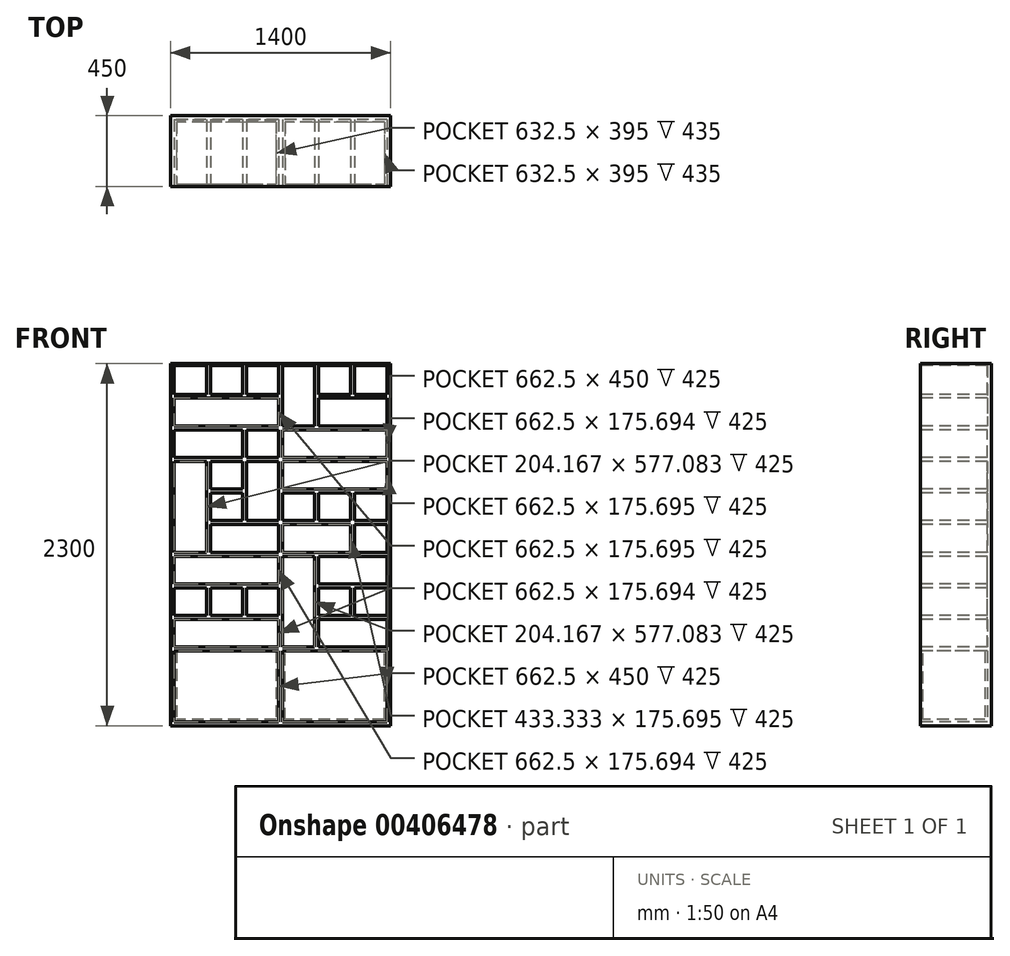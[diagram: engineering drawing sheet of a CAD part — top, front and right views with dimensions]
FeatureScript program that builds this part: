
annotation { "Feature Type Name" : "Feature", "Feature Type Description" : "" }
export const myFeature = defineFeature(function(context is Context, id is Id, definition is map)
    precondition{}
    {
        {
            var Q0;
            Q0=qCreatedBy(makeId("Front.planeOp"),FACE);
            var sketch = newSketch(context, id + "F0", { "sketchPlane" : qUnion([Q0])});
            skLineSegment(sketch, "E0.bottom", {"start": v(-700, 0) * mm, "end": v(700, 0) * mm});
            skLineSegment(sketch, "E0.top", {"start": v(-700, 2300) * mm, "end": v(700, 2300) * mm});
            skLineSegment(sketch, "E0.left", {"start": v(-700, 0) * mm, "end": v(-700, 2300) * mm});
            skLineSegment(sketch, "E0.right", {"start": v(700, 0) * mm, "end": v(700, 2300) * mm});
            skSolve(sketch);
        }
        {
            var Q0;
            Q0=qSketchRegion(id+"F0",true);
            extrude(context, id + "F1", {"entities" : qUnion([Q0]), "depth" : 450 * mm, "offsetDistance" : 25 * mm});
        }
        {
            var Q0;
            Q0=makeQuery(id+"F1.opExtrude","CAP_FACE",FACE,{"disambiguationData":[OSD([sQuery(id+"F0.wireOp",EDGE,"E0.bottom"),sQuery(id+"F0.wireOp",EDGE,"E0.top"),sQuery(id+"F0.wireOp",EDGE,"E0.left"),sQuery(id+"F0.wireOp",EDGE,"E0.right")])],"isStart":false});
            var sketch = newSketch(context, id + "F2", { "sketchPlane" : qUnion([Q0])});
            skLineSegment(sketch, "E1", {"start": v(0, 2300) * mm, "end": v(0, 0) * mm, "construction": true});
            skLineSegment(sketch, "E2.bottom", {"start": v(-675, 25) * mm, "end": v(-12.5, 25) * mm});
            skLineSegment(sketch, "E2.top", {"start": v(-675, 475) * mm, "end": v(-12.5, 475) * mm});
            skLineSegment(sketch, "E2.left", {"start": v(-675, 25) * mm, "end": v(-675, 475) * mm});
            skLineSegment(sketch, "E2.right", {"start": v(-12.5, 25) * mm, "end": v(-12.5, 475) * mm});
            skLineSegment(sketch, "E3.bottom", {"start": v(12.5, 475) * mm, "end": v(675, 475) * mm});
            skLineSegment(sketch, "E3.top", {"start": v(12.5, 25) * mm, "end": v(675, 25) * mm});
            skLineSegment(sketch, "E3.left", {"start": v(12.5, 475) * mm, "end": v(12.5, 25) * mm});
            skLineSegment(sketch, "E3.right", {"start": v(675, 475) * mm, "end": v(675, 25) * mm});
            skLineSegment(sketch, "E4", {"start": v(-700, 487.5) * mm, "end": v(700, 487.5) * mm, "construction": true});
            skLineSegment(sketch, "E5", {"start": v(-700, 1089.58) * mm, "end": v(700, 1089.58) * mm, "construction": true});
            skLineSegment(sketch, "E6", {"start": v(-700, 1691.67) * mm, "end": v(700, 1691.67) * mm, "construction": true});
            skLineSegment(sketch, "E7", {"start": v(-700, 2293.75) * mm, "end": v(700, 2293.75) * mm, "construction": true});
            skLineSegment(sketch, "E8.bottom", {"start": v(-675, 2287.5) * mm, "end": v(-12.5, 2287.5) * mm, "construction": true});
            skLineSegment(sketch, "E8.top", {"start": v(-675, 1704.17) * mm, "end": v(-12.5, 1704.17) * mm, "construction": true});
            skLineSegment(sketch, "E8.left", {"start": v(-675, 2287.5) * mm, "end": v(-675, 1704.17) * mm, "construction": true});
            skLineSegment(sketch, "E8.right", {"start": v(-12.5, 2287.5) * mm, "end": v(-12.5, 1704.17) * mm, "construction": true});
            skLineSegment(sketch, "E9.bottom", {"start": v(-675, 1679.17) * mm, "end": v(-12.5, 1679.17) * mm, "construction": true});
            skLineSegment(sketch, "E9.top", {"start": v(-675, 1102.08) * mm, "end": v(-12.5, 1102.08) * mm, "construction": true});
            skLineSegment(sketch, "E9.left", {"start": v(-675, 1679.17) * mm, "end": v(-675, 1102.08) * mm, "construction": true});
            skLineSegment(sketch, "E9.right", {"start": v(-12.5, 1679.17) * mm, "end": v(-12.5, 1102.08) * mm, "construction": true});
            skLineSegment(sketch, "E10.bottom", {"start": v(-675, 1077.08) * mm, "end": v(-12.5, 1077.08) * mm, "construction": true});
            skLineSegment(sketch, "E10.top", {"start": v(-675, 500) * mm, "end": v(-12.5, 500) * mm, "construction": true});
            skLineSegment(sketch, "E10.left", {"start": v(-675, 1077.08) * mm, "end": v(-675, 500) * mm, "construction": true});
            skLineSegment(sketch, "E10.right", {"start": v(-12.5, 1077.08) * mm, "end": v(-12.5, 500) * mm, "construction": true});
            skLineSegment(sketch, "E11.bottom", {"start": v(12.5, 1077.08) * mm, "end": v(675, 1077.08) * mm, "construction": true});
            skLineSegment(sketch, "E11.top", {"start": v(12.5, 500) * mm, "end": v(675, 500) * mm, "construction": true});
            skLineSegment(sketch, "E11.left", {"start": v(12.5, 1077.08) * mm, "end": v(12.5, 500) * mm, "construction": true});
            skLineSegment(sketch, "E11.right", {"start": v(675, 1077.08) * mm, "end": v(675, 500) * mm, "construction": true});
            skLineSegment(sketch, "E12.bottom", {"start": v(12.5, 1679.17) * mm, "end": v(675, 1679.17) * mm, "construction": true});
            skLineSegment(sketch, "E12.top", {"start": v(12.5, 1102.08) * mm, "end": v(675, 1102.08) * mm, "construction": true});
            skLineSegment(sketch, "E12.left", {"start": v(12.5, 1679.17) * mm, "end": v(12.5, 1102.08) * mm, "construction": true});
            skLineSegment(sketch, "E12.right", {"start": v(675, 1679.17) * mm, "end": v(675, 1102.08) * mm, "construction": true});
            skLineSegment(sketch, "E13.bottom", {"start": v(12.5, 2287.5) * mm, "end": v(675, 2287.5) * mm, "construction": true});
            skLineSegment(sketch, "E13.top", {"start": v(12.5, 1704.17) * mm, "end": v(675, 1704.17) * mm, "construction": true});
            skLineSegment(sketch, "E13.left", {"start": v(12.5, 2287.5) * mm, "end": v(12.5, 1704.17) * mm, "construction": true});
            skLineSegment(sketch, "E13.right", {"start": v(675, 2287.5) * mm, "end": v(675, 1704.17) * mm, "construction": true});
            skLineSegment(sketch, "E14.bottom", {"start": v(12.5, 1704.17) * mm, "end": v(675, 1704.17) * mm});
            skLineSegment(sketch, "E14.top", {"start": v(12.5, 1879.86) * mm, "end": v(675, 1879.86) * mm});
            skLineSegment(sketch, "E14.left", {"start": v(12.5, 1704.17) * mm, "end": v(12.5, 1879.86) * mm});
            skLineSegment(sketch, "E14.right", {"start": v(675, 1704.17) * mm, "end": v(675, 1879.86) * mm});
            skLineSegment(sketch, "E15.bottom", {"start": v(12.5, 1904.86) * mm, "end": v(216.67, 1904.86) * mm});
            skLineSegment(sketch, "E15.top", {"start": v(12.5, 2287.5) * mm, "end": v(216.67, 2287.5) * mm});
            skLineSegment(sketch, "E15.left", {"start": v(12.5, 1904.86) * mm, "end": v(12.5, 2287.5) * mm});
            skLineSegment(sketch, "E15.right", {"start": v(216.67, 1904.86) * mm, "end": v(216.67, 2287.5) * mm});
            skLineSegment(sketch, "E16.bottom", {"start": v(241.67, 1904.86) * mm, "end": v(675, 1904.86) * mm});
            skLineSegment(sketch, "E16.top", {"start": v(241.67, 2080.56) * mm, "end": v(675, 2080.56) * mm});
            skLineSegment(sketch, "E16.left", {"start": v(241.67, 1904.86) * mm, "end": v(241.67, 2080.56) * mm});
            skLineSegment(sketch, "E16.right", {"start": v(675, 1904.86) * mm, "end": v(675, 2080.56) * mm});
            skLineSegment(sketch, "E17.bottom", {"start": v(241.67, 2105.56) * mm, "end": v(445.83, 2105.56) * mm});
            skLineSegment(sketch, "E17.top", {"start": v(241.67, 2287.5) * mm, "end": v(445.83, 2287.5) * mm});
            skLineSegment(sketch, "E17.left", {"start": v(241.67, 2105.56) * mm, "end": v(241.67, 2287.5) * mm});
            skLineSegment(sketch, "E17.right", {"start": v(445.83, 2105.56) * mm, "end": v(445.83, 2287.5) * mm});
            skLineSegment(sketch, "E18.bottom", {"start": v(470.83, 2287.5) * mm, "end": v(675, 2287.5) * mm});
            skLineSegment(sketch, "E18.top", {"start": v(470.83, 2105.56) * mm, "end": v(675, 2105.56) * mm});
            skLineSegment(sketch, "E18.left", {"start": v(470.83, 2287.5) * mm, "end": v(470.83, 2105.56) * mm});
            skLineSegment(sketch, "E18.right", {"start": v(675, 2287.5) * mm, "end": v(675, 2105.56) * mm});
            skLineSegment(sketch, "E19", {"start": v(229.17, 2293.75) * mm, "end": v(229.17, 1691.67) * mm, "construction": true});
            skLineSegment(sketch, "E20", {"start": v(458.33, 2293.75) * mm, "end": v(458.33, 1691.67) * mm, "construction": true});
            skLineSegment(sketch, "E21", {"start": v(687.5, 2293.75) * mm, "end": v(687.5, 1691.67) * mm, "construction": true});
            skLineSegment(sketch, "E22", {"start": v(0, 1892.36) * mm, "end": v(687.5, 1892.36) * mm, "construction": true});
            skLineSegment(sketch, "E23", {"start": v(687.5, 2093.06) * mm, "end": v(0, 2093.06) * mm, "construction": true});
            skLineSegment(sketch, "E24.bottom", {"start": v(-12.5, 1904.86) * mm, "end": v(-675, 1904.86) * mm});
            skLineSegment(sketch, "E24.top", {"start": v(-12.5, 2080.56) * mm, "end": v(-675, 2080.56) * mm});
            skLineSegment(sketch, "E24.left", {"start": v(-12.5, 1904.86) * mm, "end": v(-12.5, 2080.56) * mm});
            skLineSegment(sketch, "E24.right", {"start": v(-675, 1904.86) * mm, "end": v(-675, 2080.56) * mm});
            skLineSegment(sketch, "E25.bottom", {"start": v(-12.5, 1879.86) * mm, "end": v(-216.67, 1879.86) * mm});
            skLineSegment(sketch, "E25.top", {"start": v(-12.5, 1704.17) * mm, "end": v(-216.67, 1704.17) * mm});
            skLineSegment(sketch, "E25.left", {"start": v(-12.5, 1879.86) * mm, "end": v(-12.5, 1704.17) * mm});
            skLineSegment(sketch, "E25.right", {"start": v(-216.67, 1879.86) * mm, "end": v(-216.67, 1704.17) * mm});
            skLineSegment(sketch, "E26.bottom", {"start": v(-675, 1879.86) * mm, "end": v(-241.67, 1879.86) * mm});
            skLineSegment(sketch, "E26.top", {"start": v(-675, 1704.17) * mm, "end": v(-241.67, 1704.17) * mm});
            skLineSegment(sketch, "E26.left", {"start": v(-675, 1879.86) * mm, "end": v(-675, 1704.17) * mm});
            skLineSegment(sketch, "E26.right", {"start": v(-241.67, 1879.86) * mm, "end": v(-241.67, 1704.17) * mm});
            skLineSegment(sketch, "E27.bottom", {"start": v(-12.5, 2287.5) * mm, "end": v(-216.67, 2287.5) * mm});
            skLineSegment(sketch, "E27.top", {"start": v(-12.5, 2105.56) * mm, "end": v(-216.67, 2105.56) * mm});
            skLineSegment(sketch, "E27.left", {"start": v(-12.5, 2287.5) * mm, "end": v(-12.5, 2105.56) * mm});
            skLineSegment(sketch, "E27.right", {"start": v(-216.67, 2287.5) * mm, "end": v(-216.67, 2105.56) * mm});
            skLineSegment(sketch, "E28.bottom", {"start": v(-241.67, 2105.56) * mm, "end": v(-445.83, 2105.56) * mm});
            skLineSegment(sketch, "E28.top", {"start": v(-241.67, 2287.5) * mm, "end": v(-445.83, 2287.5) * mm});
            skLineSegment(sketch, "E28.left", {"start": v(-241.67, 2105.56) * mm, "end": v(-241.67, 2287.5) * mm});
            skLineSegment(sketch, "E28.right", {"start": v(-445.83, 2105.56) * mm, "end": v(-445.83, 2287.5) * mm});
            skLineSegment(sketch, "E29.bottom", {"start": v(-470.83, 2287.5) * mm, "end": v(-675, 2287.5) * mm});
            skLineSegment(sketch, "E29.top", {"start": v(-470.83, 2105.56) * mm, "end": v(-675, 2105.56) * mm});
            skLineSegment(sketch, "E29.left", {"start": v(-470.83, 2287.5) * mm, "end": v(-470.83, 2105.56) * mm});
            skLineSegment(sketch, "E29.right", {"start": v(-675, 2287.5) * mm, "end": v(-675, 2105.56) * mm});
            skLineSegment(sketch, "E30.bottom", {"start": v(12.5, 1679.17) * mm, "end": v(675, 1679.17) * mm});
            skLineSegment(sketch, "E30.top", {"start": v(12.5, 1503.47) * mm, "end": v(675, 1503.47) * mm});
            skLineSegment(sketch, "E30.left", {"start": v(12.5, 1679.17) * mm, "end": v(12.5, 1503.47) * mm});
            skLineSegment(sketch, "E30.right", {"start": v(675, 1679.17) * mm, "end": v(675, 1503.47) * mm});
            skLineSegment(sketch, "E31.bottom", {"start": v(12.5, 1478.47) * mm, "end": v(216.67, 1478.47) * mm});
            skLineSegment(sketch, "E31.top", {"start": v(12.5, 1302.78) * mm, "end": v(216.67, 1302.78) * mm});
            skLineSegment(sketch, "E31.left", {"start": v(12.5, 1478.47) * mm, "end": v(12.5, 1302.78) * mm});
            skLineSegment(sketch, "E31.right", {"start": v(216.67, 1478.47) * mm, "end": v(216.67, 1302.78) * mm});
            skLineSegment(sketch, "E32.bottom", {"start": v(241.67, 1478.47) * mm, "end": v(445.83, 1478.47) * mm});
            skLineSegment(sketch, "E32.top", {"start": v(241.67, 1302.78) * mm, "end": v(445.83, 1302.78) * mm});
            skLineSegment(sketch, "E32.left", {"start": v(241.67, 1478.47) * mm, "end": v(241.67, 1302.78) * mm});
            skLineSegment(sketch, "E32.right", {"start": v(445.83, 1478.47) * mm, "end": v(445.83, 1302.78) * mm});
            skLineSegment(sketch, "E33.bottom", {"start": v(470.83, 1478.47) * mm, "end": v(675, 1478.47) * mm});
            skLineSegment(sketch, "E33.top", {"start": v(470.83, 1302.78) * mm, "end": v(675, 1302.78) * mm});
            skLineSegment(sketch, "E33.left", {"start": v(470.83, 1478.47) * mm, "end": v(470.83, 1302.78) * mm});
            skLineSegment(sketch, "E33.right", {"start": v(675, 1478.47) * mm, "end": v(675, 1302.78) * mm});
            skLineSegment(sketch, "E34.bottom", {"start": v(12.5, 1277.78) * mm, "end": v(445.83, 1277.78) * mm});
            skLineSegment(sketch, "E34.top", {"start": v(12.5, 1102.08) * mm, "end": v(445.83, 1102.08) * mm});
            skLineSegment(sketch, "E34.left", {"start": v(12.5, 1277.78) * mm, "end": v(12.5, 1102.08) * mm});
            skLineSegment(sketch, "E34.right", {"start": v(445.83, 1277.78) * mm, "end": v(445.83, 1102.08) * mm});
            skLineSegment(sketch, "E35.bottom", {"start": v(470.83, 1277.78) * mm, "end": v(675, 1277.78) * mm});
            skLineSegment(sketch, "E35.top", {"start": v(470.83, 1102.08) * mm, "end": v(675, 1102.08) * mm});
            skLineSegment(sketch, "E35.left", {"start": v(470.83, 1277.78) * mm, "end": v(470.83, 1102.08) * mm});
            skLineSegment(sketch, "E35.right", {"start": v(675, 1277.78) * mm, "end": v(675, 1102.08) * mm});
            skLineSegment(sketch, "E36.bottom", {"start": v(-675, 1102.08) * mm, "end": v(-470.83, 1102.08) * mm});
            skLineSegment(sketch, "E36.top", {"start": v(-675, 1679.17) * mm, "end": v(-470.83, 1679.17) * mm});
            skLineSegment(sketch, "E36.left", {"start": v(-675, 1102.08) * mm, "end": v(-675, 1679.17) * mm});
            skLineSegment(sketch, "E36.right", {"start": v(-470.83, 1102.08) * mm, "end": v(-470.83, 1679.17) * mm});
            skLineSegment(sketch, "E37.bottom", {"start": v(-12.5, 1277.78) * mm, "end": v(-445.83, 1277.78) * mm});
            skLineSegment(sketch, "E37.top", {"start": v(-12.5, 1102.08) * mm, "end": v(-445.83, 1102.08) * mm});
            skLineSegment(sketch, "E37.left", {"start": v(-12.5, 1277.78) * mm, "end": v(-12.5, 1102.08) * mm});
            skLineSegment(sketch, "E37.right", {"start": v(-445.83, 1277.78) * mm, "end": v(-445.83, 1102.08) * mm});
            skLineSegment(sketch, "E38.bottom", {"start": v(-12.5, 1679.17) * mm, "end": v(-216.67, 1679.17) * mm});
            skLineSegment(sketch, "E38.top", {"start": v(-12.5, 1302.78) * mm, "end": v(-216.67, 1302.78) * mm});
            skLineSegment(sketch, "E38.left", {"start": v(-12.5, 1679.17) * mm, "end": v(-12.5, 1302.78) * mm});
            skLineSegment(sketch, "E38.right", {"start": v(-216.67, 1679.17) * mm, "end": v(-216.67, 1302.78) * mm});
            skLineSegment(sketch, "E39.bottom", {"start": v(-445.83, 1302.78) * mm, "end": v(-241.67, 1302.78) * mm});
            skLineSegment(sketch, "E39.top", {"start": v(-445.83, 1478.47) * mm, "end": v(-241.67, 1478.47) * mm});
            skLineSegment(sketch, "E39.left", {"start": v(-445.83, 1302.78) * mm, "end": v(-445.83, 1478.47) * mm});
            skLineSegment(sketch, "E39.right", {"start": v(-241.67, 1302.78) * mm, "end": v(-241.67, 1478.47) * mm});
            skLineSegment(sketch, "E40.bottom", {"start": v(-445.83, 1679.17) * mm, "end": v(-241.67, 1679.17) * mm});
            skLineSegment(sketch, "E40.top", {"start": v(-445.83, 1503.47) * mm, "end": v(-241.67, 1503.47) * mm});
            skLineSegment(sketch, "E40.left", {"start": v(-445.83, 1679.17) * mm, "end": v(-445.83, 1503.47) * mm});
            skLineSegment(sketch, "E40.right", {"start": v(-241.67, 1679.17) * mm, "end": v(-241.67, 1503.47) * mm});
            skLineSegment(sketch, "E41.bottom", {"start": v(-675, 1077.08) * mm, "end": v(-12.5, 1077.08) * mm});
            skLineSegment(sketch, "E41.top", {"start": v(-675, 901.39) * mm, "end": v(-12.5, 901.39) * mm});
            skLineSegment(sketch, "E41.left", {"start": v(-675, 1077.08) * mm, "end": v(-675, 901.39) * mm});
            skLineSegment(sketch, "E41.right", {"start": v(-12.5, 1077.08) * mm, "end": v(-12.5, 901.39) * mm});
            skLineSegment(sketch, "E42.bottom", {"start": v(-12.5, 500) * mm, "end": v(-675, 500) * mm});
            skLineSegment(sketch, "E42.top", {"start": v(-12.5, 675.7) * mm, "end": v(-675, 675.7) * mm});
            skLineSegment(sketch, "E42.left", {"start": v(-12.5, 500) * mm, "end": v(-12.5, 675.7) * mm});
            skLineSegment(sketch, "E42.right", {"start": v(-675, 500) * mm, "end": v(-675, 675.7) * mm});
            skLineSegment(sketch, "E43.bottom", {"start": v(-675, 876.39) * mm, "end": v(-470.83, 876.39) * mm});
            skLineSegment(sketch, "E43.top", {"start": v(-675, 700.7) * mm, "end": v(-470.83, 700.7) * mm});
            skLineSegment(sketch, "E43.left", {"start": v(-675, 876.39) * mm, "end": v(-675, 700.7) * mm});
            skLineSegment(sketch, "E43.right", {"start": v(-470.83, 876.39) * mm, "end": v(-470.83, 700.7) * mm});
            skLineSegment(sketch, "E44.bottom", {"start": v(-216.67, 876.39) * mm, "end": v(-12.5, 876.39) * mm});
            skLineSegment(sketch, "E44.top", {"start": v(-216.67, 700.7) * mm, "end": v(-12.5, 700.7) * mm});
            skLineSegment(sketch, "E44.left", {"start": v(-216.67, 876.39) * mm, "end": v(-216.67, 700.7) * mm});
            skLineSegment(sketch, "E44.right", {"start": v(-12.5, 876.39) * mm, "end": v(-12.5, 700.7) * mm});
            skLineSegment(sketch, "E45.bottom", {"start": v(-445.83, 876.39) * mm, "end": v(-241.67, 876.39) * mm});
            skLineSegment(sketch, "E45.top", {"start": v(-445.83, 700.7) * mm, "end": v(-241.67, 700.7) * mm});
            skLineSegment(sketch, "E45.left", {"start": v(-445.83, 876.39) * mm, "end": v(-445.83, 700.7) * mm});
            skLineSegment(sketch, "E45.right", {"start": v(-241.67, 876.39) * mm, "end": v(-241.67, 700.7) * mm});
            skLineSegment(sketch, "E46.bottom", {"start": v(12.5, 1077.08) * mm, "end": v(216.67, 1077.08) * mm});
            skLineSegment(sketch, "E46.top", {"start": v(12.5, 500) * mm, "end": v(216.67, 500) * mm});
            skLineSegment(sketch, "E46.left", {"start": v(12.5, 1077.08) * mm, "end": v(12.5, 500) * mm});
            skLineSegment(sketch, "E46.right", {"start": v(216.67, 1077.08) * mm, "end": v(216.67, 500) * mm});
            skLineSegment(sketch, "E47.bottom", {"start": v(241.67, 1077.08) * mm, "end": v(675, 1077.08) * mm});
            skLineSegment(sketch, "E47.top", {"start": v(241.67, 901.39) * mm, "end": v(675, 901.39) * mm});
            skLineSegment(sketch, "E47.left", {"start": v(241.67, 1077.08) * mm, "end": v(241.67, 901.39) * mm});
            skLineSegment(sketch, "E47.right", {"start": v(675, 1077.08) * mm, "end": v(675, 901.39) * mm});
            skLineSegment(sketch, "E48.bottom", {"start": v(241.67, 500) * mm, "end": v(675, 500) * mm});
            skLineSegment(sketch, "E48.top", {"start": v(241.67, 675.7) * mm, "end": v(675, 675.7) * mm});
            skLineSegment(sketch, "E48.left", {"start": v(241.67, 500) * mm, "end": v(241.67, 675.7) * mm});
            skLineSegment(sketch, "E48.right", {"start": v(675, 500) * mm, "end": v(675, 675.7) * mm});
            skLineSegment(sketch, "E49.bottom", {"start": v(241.67, 876.39) * mm, "end": v(445.83, 876.39) * mm});
            skLineSegment(sketch, "E49.top", {"start": v(241.67, 700.7) * mm, "end": v(445.83, 700.7) * mm});
            skLineSegment(sketch, "E49.left", {"start": v(241.67, 876.39) * mm, "end": v(241.67, 700.7) * mm});
            skLineSegment(sketch, "E49.right", {"start": v(445.83, 876.39) * mm, "end": v(445.83, 700.7) * mm});
            skLineSegment(sketch, "E50.bottom", {"start": v(470.83, 876.39) * mm, "end": v(675, 876.39) * mm});
            skLineSegment(sketch, "E50.top", {"start": v(470.83, 700.7) * mm, "end": v(675, 700.7) * mm});
            skLineSegment(sketch, "E50.left", {"start": v(470.83, 876.39) * mm, "end": v(470.83, 700.7) * mm});
            skLineSegment(sketch, "E50.right", {"start": v(675, 876.39) * mm, "end": v(675, 700.7) * mm});
            skSolve(sketch);
        }
        {
            var Q0;
            Q0=makeQuery(id+"F2.imprint","IMPRINT",FACE,{"disambiguationData":[TD([[makeQuery(id+"F2.imprint","IMPRINT",EDGE,{"derivedFrom":sQuery(id+"F2.wireOp",EDGE,"E29.bottom")}),1.0]])]});
            var Q1;
            Q1=makeQuery(id+"F2.imprint","IMPRINT",FACE,{"disambiguationData":[TD([[makeQuery(id+"F2.imprint","IMPRINT",EDGE,{"derivedFrom":sQuery(id+"F2.wireOp",EDGE,"E28.bottom")}),-1.0]])]});
            var Q2;
            Q2=makeQuery(id+"F2.imprint","IMPRINT",FACE,{"disambiguationData":[TD([[makeQuery(id+"F2.imprint","IMPRINT",EDGE,{"derivedFrom":sQuery(id+"F2.wireOp",EDGE,"E27.bottom")}),1.0]])]});
            var Q3;
            Q3=makeQuery(id+"F2.imprint","IMPRINT",FACE,{"disambiguationData":[TD([[makeQuery(id+"F2.imprint","IMPRINT",EDGE,{"derivedFrom":sQuery(id+"F2.wireOp",EDGE,"E15.bottom")}),1.0]])]});
            var Q4;
            Q4=makeQuery(id+"F2.imprint","IMPRINT",FACE,{"disambiguationData":[TD([[makeQuery(id+"F2.imprint","IMPRINT",EDGE,{"derivedFrom":sQuery(id+"F2.wireOp",EDGE,"E17.bottom")}),1.0]])]});
            var Q5;
            Q5=makeQuery(id+"F2.imprint","IMPRINT",FACE,{"disambiguationData":[TD([[makeQuery(id+"F2.imprint","IMPRINT",EDGE,{"derivedFrom":sQuery(id+"F2.wireOp",EDGE,"E18.bottom")}),-1.0]])]});
            var Q6;
            Q6=makeQuery(id+"F2.imprint","IMPRINT",FACE,{"disambiguationData":[TD([[makeQuery(id+"F2.imprint","IMPRINT",EDGE,{"derivedFrom":sQuery(id+"F2.wireOp",EDGE,"E24.bottom")}),-1.0]])]});
            var Q7;
            Q7=makeQuery(id+"F2.imprint","IMPRINT",FACE,{"disambiguationData":[TD([[makeQuery(id+"F2.imprint","IMPRINT",EDGE,{"derivedFrom":sQuery(id+"F2.wireOp",EDGE,"E16.bottom")}),1.0]])]});
            var Q8;
            Q8=makeQuery(id+"F2.imprint","IMPRINT",FACE,{"disambiguationData":[TD([[makeQuery(id+"F2.imprint","IMPRINT",EDGE,{"derivedFrom":sQuery(id+"F2.wireOp",EDGE,"E26.bottom")}),-1.0]])]});
            var Q9;
            Q9=makeQuery(id+"F2.imprint","IMPRINT",FACE,{"disambiguationData":[TD([[makeQuery(id+"F2.imprint","IMPRINT",EDGE,{"derivedFrom":sQuery(id+"F2.wireOp",EDGE,"E25.bottom")}),1.0]])]});
            var Q10;
            Q10=makeQuery(id+"F2.imprint","IMPRINT",FACE,{"disambiguationData":[TD([[makeQuery(id+"F2.imprint","IMPRINT",EDGE,{"derivedFrom":sQuery(id+"F2.wireOp",EDGE,"E14.bottom")}),1.0]])]});
            var Q11;
            Q11=makeQuery(id+"F2.imprint","IMPRINT",FACE,{"disambiguationData":[TD([[makeQuery(id+"F2.imprint","IMPRINT",EDGE,{"derivedFrom":sQuery(id+"F2.wireOp",EDGE,"E36.bottom")}),1.0]])]});
            var Q12;
            Q12=makeQuery(id+"F2.imprint","IMPRINT",FACE,{"disambiguationData":[TD([[makeQuery(id+"F2.imprint","IMPRINT",EDGE,{"derivedFrom":sQuery(id+"F2.wireOp",EDGE,"E40.bottom")}),-1.0]])]});
            var Q13;
            Q13=makeQuery(id+"F2.imprint","IMPRINT",FACE,{"disambiguationData":[TD([[makeQuery(id+"F2.imprint","IMPRINT",EDGE,{"derivedFrom":sQuery(id+"F2.wireOp",EDGE,"E39.bottom")}),1.0]])]});
            var Q14;
            Q14=makeQuery(id+"F2.imprint","IMPRINT",FACE,{"disambiguationData":[TD([[makeQuery(id+"F2.imprint","IMPRINT",EDGE,{"derivedFrom":sQuery(id+"F2.wireOp",EDGE,"E37.bottom")}),1.0]])]});
            var Q15;
            Q15=makeQuery(id+"F2.imprint","IMPRINT",FACE,{"disambiguationData":[TD([[makeQuery(id+"F2.imprint","IMPRINT",EDGE,{"derivedFrom":sQuery(id+"F2.wireOp",EDGE,"E38.bottom")}),1.0]])]});
            var Q16;
            Q16=makeQuery(id+"F2.imprint","IMPRINT",FACE,{"disambiguationData":[TD([[makeQuery(id+"F2.imprint","IMPRINT",EDGE,{"derivedFrom":sQuery(id+"F2.wireOp",EDGE,"E30.bottom")}),-1.0]])]});
            var Q17;
            Q17=makeQuery(id+"F2.imprint","IMPRINT",FACE,{"disambiguationData":[TD([[makeQuery(id+"F2.imprint","IMPRINT",EDGE,{"derivedFrom":sQuery(id+"F2.wireOp",EDGE,"E31.bottom")}),-1.0]])]});
            var Q18;
            Q18=makeQuery(id+"F2.imprint","IMPRINT",FACE,{"disambiguationData":[TD([[makeQuery(id+"F2.imprint","IMPRINT",EDGE,{"derivedFrom":sQuery(id+"F2.wireOp",EDGE,"E32.bottom")}),-1.0]])]});
            var Q19;
            Q19=makeQuery(id+"F2.imprint","IMPRINT",FACE,{"disambiguationData":[TD([[makeQuery(id+"F2.imprint","IMPRINT",EDGE,{"derivedFrom":sQuery(id+"F2.wireOp",EDGE,"E33.bottom")}),-1.0]])]});
            var Q20;
            Q20=makeQuery(id+"F2.imprint","IMPRINT",FACE,{"disambiguationData":[TD([[makeQuery(id+"F2.imprint","IMPRINT",EDGE,{"derivedFrom":sQuery(id+"F2.wireOp",EDGE,"E34.bottom")}),-1.0]])]});
            var Q21;
            Q21=makeQuery(id+"F2.imprint","IMPRINT",FACE,{"disambiguationData":[TD([[makeQuery(id+"F2.imprint","IMPRINT",EDGE,{"derivedFrom":sQuery(id+"F2.wireOp",EDGE,"E35.bottom")}),-1.0]])]});
            var Q22;
            Q22=makeQuery(id+"F2.imprint","IMPRINT",FACE,{"disambiguationData":[TD([[makeQuery(id+"F2.imprint","IMPRINT",EDGE,{"derivedFrom":sQuery(id+"F2.wireOp",EDGE,"E41.bottom")}),-1.0]])]});
            var Q23;
            Q23=makeQuery(id+"F2.imprint","IMPRINT",FACE,{"disambiguationData":[TD([[makeQuery(id+"F2.imprint","IMPRINT",EDGE,{"derivedFrom":sQuery(id+"F2.wireOp",EDGE,"E43.bottom")}),-1.0]])]});
            var Q24;
            Q24=makeQuery(id+"F2.imprint","IMPRINT",FACE,{"disambiguationData":[TD([[makeQuery(id+"F2.imprint","IMPRINT",EDGE,{"derivedFrom":sQuery(id+"F2.wireOp",EDGE,"E45.bottom")}),-1.0]])]});
            var Q25;
            Q25=makeQuery(id+"F2.imprint","IMPRINT",FACE,{"disambiguationData":[TD([[makeQuery(id+"F2.imprint","IMPRINT",EDGE,{"derivedFrom":sQuery(id+"F2.wireOp",EDGE,"E44.bottom")}),-1.0]])]});
            var Q26;
            Q26=makeQuery(id+"F2.imprint","IMPRINT",FACE,{"disambiguationData":[TD([[makeQuery(id+"F2.imprint","IMPRINT",EDGE,{"derivedFrom":sQuery(id+"F2.wireOp",EDGE,"E42.bottom")}),-1.0]])]});
            var Q27;
            Q27=makeQuery(id+"F2.imprint","IMPRINT",FACE,{"disambiguationData":[TD([[makeQuery(id+"F2.imprint","IMPRINT",EDGE,{"derivedFrom":sQuery(id+"F2.wireOp",EDGE,"E46.bottom")}),-1.0]])]});
            var Q28;
            Q28=makeQuery(id+"F2.imprint","IMPRINT",FACE,{"disambiguationData":[TD([[makeQuery(id+"F2.imprint","IMPRINT",EDGE,{"derivedFrom":sQuery(id+"F2.wireOp",EDGE,"E47.bottom")}),-1.0]])]});
            var Q29;
            Q29=makeQuery(id+"F2.imprint","IMPRINT",FACE,{"disambiguationData":[TD([[makeQuery(id+"F2.imprint","IMPRINT",EDGE,{"derivedFrom":sQuery(id+"F2.wireOp",EDGE,"E49.bottom")}),-1.0]])]});
            var Q30;
            Q30=makeQuery(id+"F2.imprint","IMPRINT",FACE,{"disambiguationData":[TD([[makeQuery(id+"F2.imprint","IMPRINT",EDGE,{"derivedFrom":sQuery(id+"F2.wireOp",EDGE,"E50.bottom")}),-1.0]])]});
            var Q31;
            Q31=makeQuery(id+"F2.imprint","IMPRINT",FACE,{"disambiguationData":[TD([[makeQuery(id+"F2.imprint","IMPRINT",EDGE,{"derivedFrom":sQuery(id+"F2.wireOp",EDGE,"E48.bottom")}),1.0]])]});
            var Q32;
            Q32=makeQuery(id+"F2.imprint","IMPRINT",FACE,{"disambiguationData":[TD([[makeQuery(id+"F2.imprint","IMPRINT",EDGE,{"derivedFrom":sQuery(id+"F2.wireOp",EDGE,"E2.bottom")}),1.0]])]});
            var Q33;
            Q33=makeQuery(id+"F2.imprint","IMPRINT",FACE,{"disambiguationData":[TD([[makeQuery(id+"F2.imprint","IMPRINT",EDGE,{"derivedFrom":sQuery(id+"F2.wireOp",EDGE,"E3.bottom")}),-1.0]])]});
            extrude(context, id + "F3", {"entities" : qUnion([Q0, Q1, Q2, Q3, Q4, Q5, Q6, Q7, Q8, Q9, Q10, Q11, Q12, Q13, Q14, Q15, Q16, Q17, Q18, Q19, Q20, Q21, Q22, Q23, Q24, Q25, Q26, Q27, Q28, Q29, Q30, Q31, Q32, Q33]), "operationType" : NewBodyOperationType.REMOVE, "endBound" : BoundingType.UP_TO_NEXT, "oppositeDirection" : true, "depth" : 25 * mm, "hasOffset" : true, "offsetDistance" : 25 * mm});
        }
        {
            var Q0;
            Q0=makeQuery(id+"F2.imprint","IMPRINT",FACE,{"disambiguationData":[TD([[makeQuery(id+"F2.imprint","IMPRINT",EDGE,{"derivedFrom":sQuery(id+"F2.wireOp",EDGE,"E2.bottom")}),1.0]])]});
            var Q1;
            Q1=makeQuery(id+"F2.imprint","IMPRINT",FACE,{"disambiguationData":[TD([[makeQuery(id+"F2.imprint","IMPRINT",EDGE,{"derivedFrom":sQuery(id+"F2.wireOp",EDGE,"E3.bottom")}),-1.0]])]});
            extrude(context, id + "F4", {"entities" : qUnion([Q0, Q1]), "endBound" : BoundingType.UP_TO_NEXT, "oppositeDirection" : true, "depth" : 25 * mm, "offsetDistance" : 25 * mm});
        }
        {
            var Q0;
            Q0=makeQuery(id+"F4.opExtrude","SWEPT_FACE",FACE,{"disambiguationData":[OSD([sQuery(id+"F2.wireOp",EDGE,"E2.top")])]});
            var Q1;
            Q1=makeQuery(id+"F4.opExtrude","SWEPT_FACE",FACE,{"disambiguationData":[OSD([sQuery(id+"F2.wireOp",EDGE,"E3.bottom")])]});
            shell(context, id + "F5", {"entities" : qUnion([Q0, Q1]), "thickness" : 15 * mm});
        }
    });
